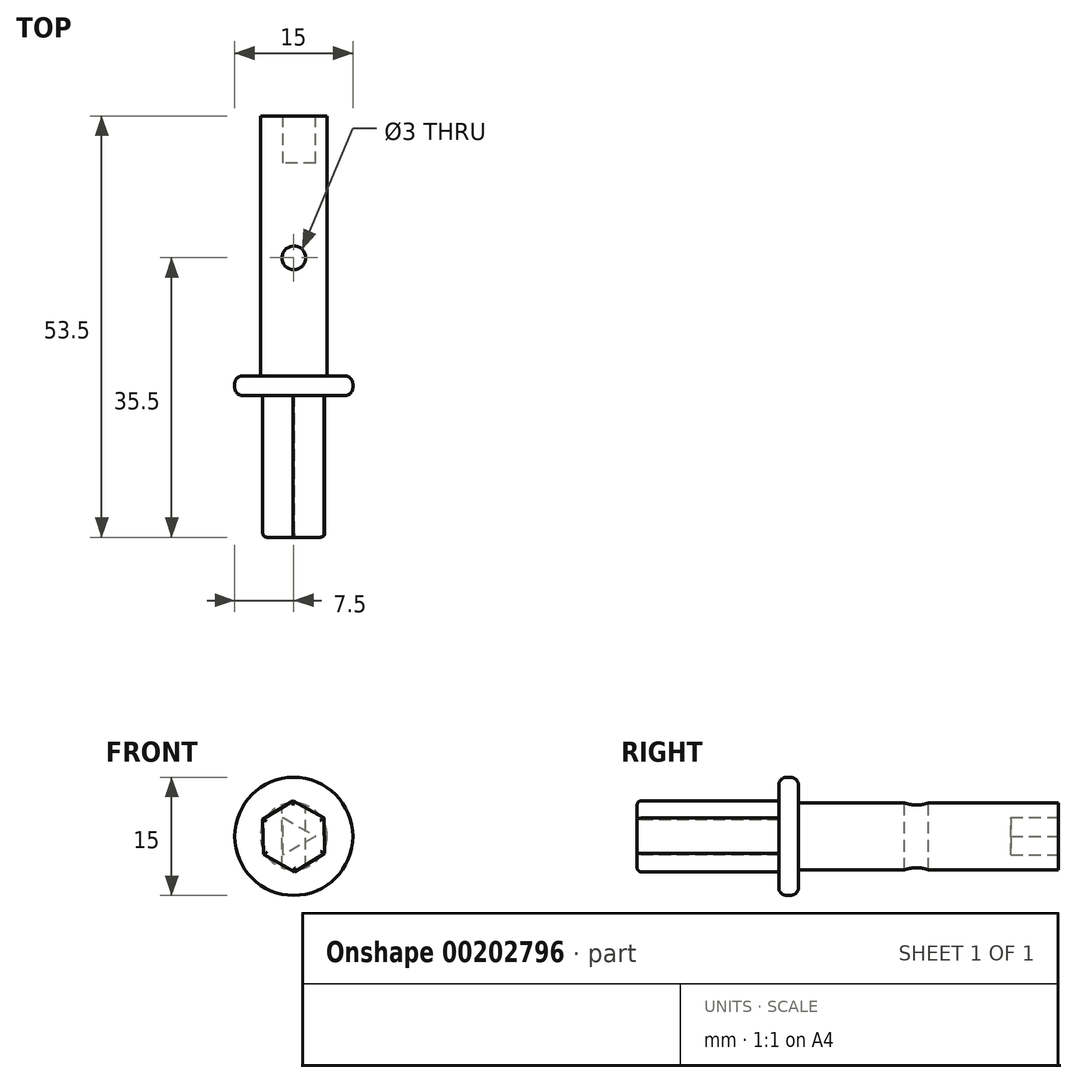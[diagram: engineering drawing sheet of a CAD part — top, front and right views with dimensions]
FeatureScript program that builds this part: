
annotation { "Feature Type Name" : "Feature", "Feature Type Description" : "" }
export const myFeature = defineFeature(function(context is Context, id is Id, definition is map)
    precondition{}
    {
        {
            var Q0;
            Q0=qCreatedBy(makeId("Front.planeOp"),FACE);
            var sketch = newSketch(context, id + "F0", { "sketchPlane" : qUnion([Q0])});
            skCircle(sketch, "E0", {"center": v(0, 0) * mm, "radius": 4.25 * mm});
            skCircle(sketch, "E1.0", {"center": v(0, 0) * mm, "radius": 2.75 * mm, "construction": true});
            skLineSegment(sketch, "E2.0", {"start": v(2.75, 0) * mm, "end": v(-1.38, -2.38) * mm});
            skLineSegment(sketch, "E2.1", {"start": v(-1.37, -2.38) * mm, "end": v(-1.37, 2.38) * mm});
            skLineSegment(sketch, "E2.2", {"start": v(-1.37, 2.38) * mm, "end": v(2.75, 0) * mm});
            skSolve(sketch);
        }
        {
            var Q0;
            Q0=makeQuery(id+"F0.imprint","IMPRINT",FACE,{"disambiguationData":[TD([[makeQuery(id+"F0.imprint","IMPRINT",EDGE,{"derivedFrom":sQuery(id+"F0.wireOp",EDGE,"E0")}),1.0]])]});
            var Q1;
            Q1=makeQuery(id+"F0.imprint","IMPRINT",FACE,{"disambiguationData":[TD([[makeQuery(id+"F0.imprint","IMPRINT",EDGE,{"derivedFrom":sQuery(id+"F0.wireOp",EDGE,"E2.0")}),-1.0]])]});
            extrude(context, id + "F1", {"entities" : qUnion([Q0, Q1]), "depth" : 33 * mm});
        }
        {
            var Q0;
            Q0=makeQuery(id+"F0.imprint","IMPRINT",FACE,{"disambiguationData":[TD([[makeQuery(id+"F0.imprint","IMPRINT",EDGE,{"derivedFrom":sQuery(id+"F0.wireOp",EDGE,"E2.0")}),-1.0]])]});
            extrude(context, id + "F2", {"entities" : qUnion([Q0]), "operationType" : NewBodyOperationType.REMOVE, "depth" : 6 * mm});
        }
        {
            var Q0;
            Q0=makeQuery(id+"F1.opExtrude","CAP_FACE",FACE,{"disambiguationData":[OSD([sQuery(id+"F0.wireOp",EDGE,"E0")])],"isStart":false});
            var sketch = newSketch(context, id + "F3", { "sketchPlane" : qUnion([Q0])});
            skCircle(sketch, "E3", {"center": v(0, 0) * mm, "radius": 7.5 * mm});
            skSolve(sketch);
        }
        {
            var Q0;
            Q0=makeQuery(id+"F3.imprint","IMPRINT",FACE,{"disambiguationData":[TD([[makeQuery(id+"F3.imprint","IMPRINT",EDGE,{"derivedFrom":sQuery(id+"F3.wireOp",EDGE,"E3")}),1.0]])]});
            var Q1;
            Q1=makeQuery(id+"F3.imprint","IMPRINT",FACE,{"disambiguationData":[TD([[makeQuery(id+"F3.imprint","IMPRINT",EDGE,{"derivedFrom":makeQuery(id+"F1.opExtrude","CAP_EDGE",EDGE,{"disambiguationData":[OSD([sQuery(id+"F0.wireOp",EDGE,"E0")])],"isStart":false})}),1.0]])]});
            extrude(context, id + "F4", {"entities" : qUnion([Q0, Q1]), "operationType" : NewBodyOperationType.ADD, "depth" : 2.5 * mm});
        }
        {
            var Q0;
            Q0=makeQuery(id+"F4.opExtrude","CAP_FACE",FACE,{"disambiguationData":[OSD([sQuery(id+"F3.wireOp",EDGE,"E3")])],"isStart":false});
            var sketch = newSketch(context, id + "F5", { "sketchPlane" : qUnion([Q0])});
            skCircle(sketch, "E4", {"center": v(0, 0) * mm, "radius": 4.5 * mm, "construction": true});
            skLineSegment(sketch, "E5.0", {"start": v(3.93, -2.18) * mm, "end": v(0.08, -4.5) * mm});
            skLineSegment(sketch, "E5.1", {"start": v(0.08, -4.5) * mm, "end": v(-3.86, -2.32) * mm});
            skLineSegment(sketch, "E5.2", {"start": v(-3.86, -2.32) * mm, "end": v(-3.93, 2.18) * mm});
            skLineSegment(sketch, "E5.3", {"start": v(-3.93, 2.18) * mm, "end": v(-0.08, 4.5) * mm});
            skLineSegment(sketch, "E5.4", {"start": v(-0.08, 4.5) * mm, "end": v(3.86, 2.32) * mm});
            skLineSegment(sketch, "E5.5", {"start": v(3.86, 2.32) * mm, "end": v(3.93, -2.18) * mm});
            skSolve(sketch);
        }
        {
            var Q0;
            Q0=makeQuery(id+"F5.imprint","IMPRINT",FACE,{"disambiguationData":[TD([[makeQuery(id+"F5.imprint","IMPRINT",EDGE,{"derivedFrom":sQuery(id+"F5.wireOp",EDGE,"E5.0")}),-1.0]])]});
            extrude(context, id + "F6", {"entities" : qUnion([Q0]), "operationType" : NewBodyOperationType.ADD, "depth" : 18 * mm});
        }
        {
            var Q0;
            Q0=makeQuery(id+"F6.opExtrude","CAP_EDGE",EDGE,{"disambiguationData":[OSD([sQuery(id+"F5.wireOp",EDGE,"E5.0")])],"isStart":false});
            var Q1;
            Q1=makeQuery(id+"F6.opExtrude","CAP_EDGE",EDGE,{"disambiguationData":[OSD([sQuery(id+"F5.wireOp",EDGE,"E5.1")])],"isStart":false});
            var Q2;
            Q2=makeQuery(id+"F6.opExtrude","CAP_EDGE",EDGE,{"disambiguationData":[OSD([sQuery(id+"F5.wireOp",EDGE,"E5.2")])],"isStart":false});
            var Q3;
            Q3=makeQuery(id+"F6.opExtrude","CAP_EDGE",EDGE,{"disambiguationData":[OSD([sQuery(id+"F5.wireOp",EDGE,"E5.3")])],"isStart":false});
            var Q4;
            Q4=makeQuery(id+"F6.opExtrude","CAP_EDGE",EDGE,{"disambiguationData":[OSD([sQuery(id+"F5.wireOp",EDGE,"E5.4")])],"isStart":false});
            var Q5;
            Q5=makeQuery(id+"F6.opExtrude","CAP_EDGE",EDGE,{"disambiguationData":[OSD([sQuery(id+"F5.wireOp",EDGE,"E5.5")])],"isStart":false});
            fillet(context, id + "F7", {"entities" : qUnion([Q0, Q1, Q2, Q3, Q4, Q5]), "radius" : .5 * mm, "tangentPropagation" : true, "allowEdgeOverflow" : false});
        }
        {
            var Q0;
            Q0=makeQuery(id+"F4.opExtrude","CAP_EDGE",EDGE,{"disambiguationData":[OSD([sQuery(id+"F3.wireOp",EDGE,"E3")])],"isStart":false});
            var Q1;
            Q1=makeQuery(id+"F4.opExtrude","CAP_EDGE",EDGE,{"disambiguationData":[OSD([sQuery(id+"F3.wireOp",EDGE,"E3")])],"isStart":true});
            fillet(context, id + "F8", {"entities" : qUnion([Q0, Q1]), "radius" : 1 * mm, "tangentPropagation" : true, "allowEdgeOverflow" : false});
        }
        {
            var Q0;
            Q0=qCreatedBy(makeId("Top.planeOp"),FACE);
            cPlane(context, id + "F9", {"entities" : qUnion([Q0]), "cplaneType" : CPlaneType.OFFSET, "offset" : 25 * mm, "width" : 150 * mm, "height" : 150 * mm});
        }
        {
            var Q0;
            Q0=qCreatedBy(id+"F9.planeOp",FACE);
            var sketch = newSketch(context, id + "F10", { "sketchPlane" : qUnion([Q0])});
            skCircle(sketch, "E6", {"center": v(0, -18) * mm, "radius": 1.5 * mm});
            skLineSegment(sketch, "E7", {"start": v(0, 0) * mm, "end": v(0, -18) * mm, "construction": true});
            skSolve(sketch);
        }
        {
            var Q0;
            Q0=makeQuery(id+"F10.imprint","IMPRINT",FACE,{"disambiguationData":[TD([[makeQuery(id+"F10.imprint","IMPRINT",EDGE,{"derivedFrom":sQuery(id+"F10.wireOp",EDGE,"E6")}),1.0]])]});
            extrude(context, id + "F11", {"entities" : qUnion([Q0]), "operationType" : NewBodyOperationType.REMOVE, "oppositeDirection" : true, "depth" : 40 * mm});
        }
    });
